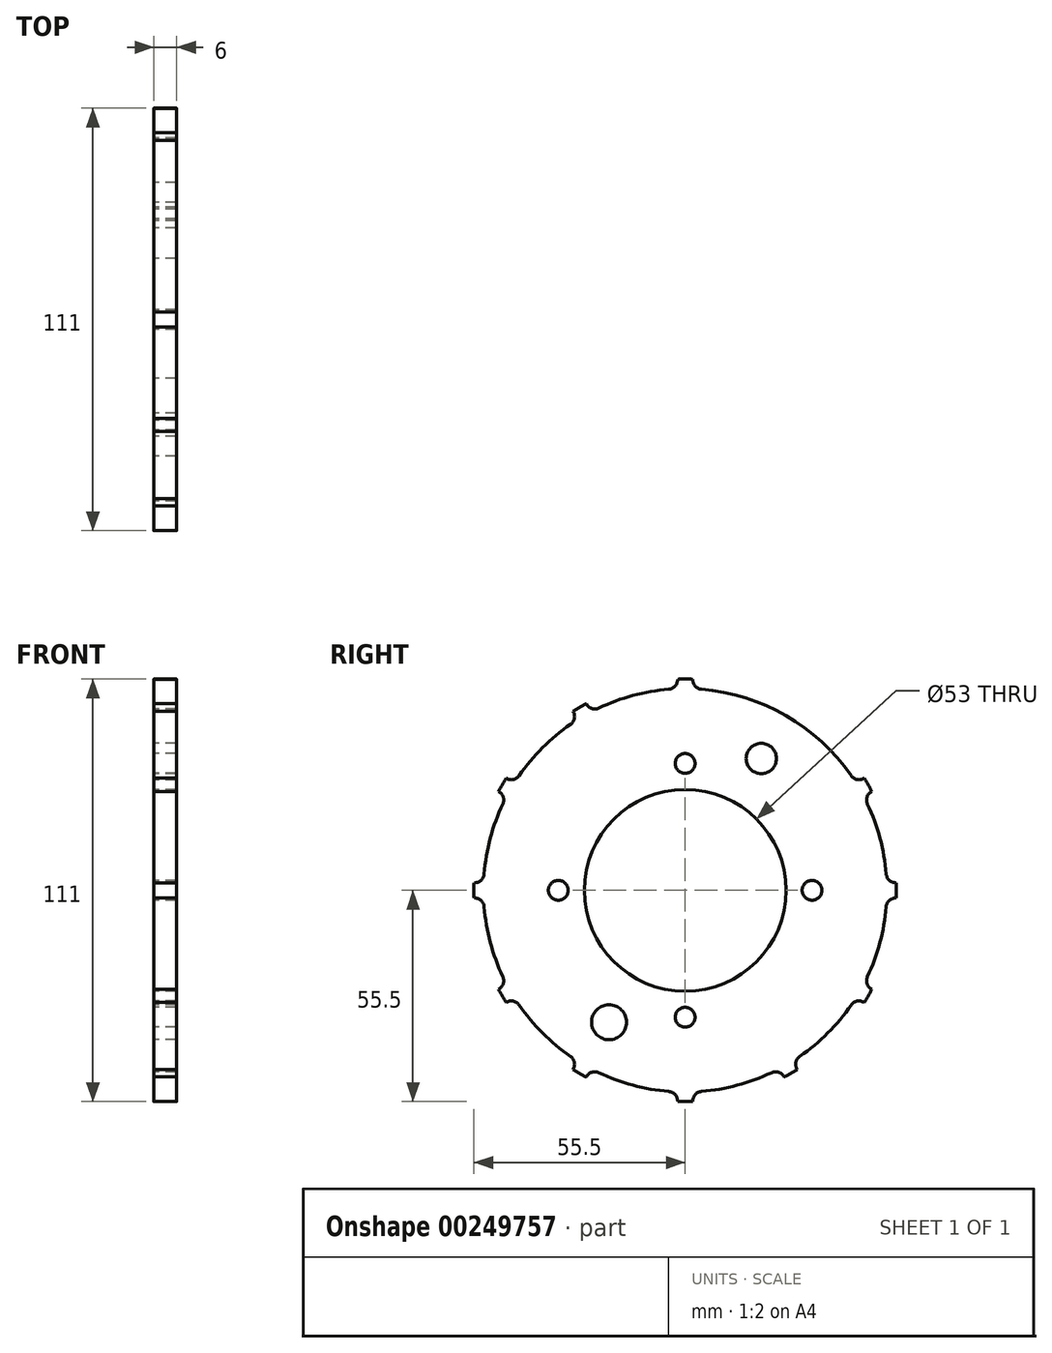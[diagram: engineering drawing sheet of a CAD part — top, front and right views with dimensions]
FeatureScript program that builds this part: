
annotation { "Feature Type Name" : "Feature", "Feature Type Description" : "" }
export const myFeature = defineFeature(function(context is Context, id is Id, definition is map)
    precondition{}
    {
        {
            var Q0;
            Q0=qCreatedBy(makeId("Right.planeOp"),FACE);
            var sketch = newSketch(context, id + "F0", { "sketchPlane" : qUnion([Q0])});
            skCircle(sketch, "E0", {"center": v(0, 0) * mm, "radius": 26.5 * mm});
            skLineSegment(sketch, "E1", {"start": v(0, 6.12) * mm, "end": v(0, -11) * mm, "construction": true});
            skCircle(sketch, "E2", {"center": v(0, 0) * mm, "radius": 53 * mm});
            skLineSegment(sketch, "E3", {"start": v(0, 0) * mm, "end": v(-20, -34.64) * mm, "construction": true});
            skCircle(sketch, "E4", {"center": v(-20, -34.64) * mm, "radius": 4.6 * mm});
            skArc(sketch, "E5", {"start": v(-6.98, 55.06) * mm, "mid": v(-4.3, 52.83) * mm, "end": v(-2, 55.46) * mm});
            skArc(sketch, "E6.1.0", {"start": v(-33.58, 44.2) * mm, "mid": v(-30.13, 43.6) * mm, "end": v(-29.46, 47.03) * mm});
            skArc(sketch, "E6.2.0", {"start": v(-51.17, 21.48) * mm, "mid": v(-47.9, 22.7) * mm, "end": v(-49.03, 26) * mm});
            skArc(sketch, "E6.3.0", {"start": v(-55.06, -6.98) * mm, "mid": v(-52.83, -4.3) * mm, "end": v(-55.46, -2) * mm});
            skArc(sketch, "E6.4.0", {"start": v(-44.2, -33.58) * mm, "mid": v(-43.6, -30.13) * mm, "end": v(-47.03, -29.46) * mm});
            skArc(sketch, "E6.5.0", {"start": v(-21.48, -51.17) * mm, "mid": v(-22.7, -47.9) * mm, "end": v(-26, -49.03) * mm});
            skArc(sketch, "E6.6.0", {"start": v(6.98, -55.06) * mm, "mid": v(4.3, -52.83) * mm, "end": v(2, -55.46) * mm});
            skArc(sketch, "E6.7.0", {"start": v(33.58, -44.2) * mm, "mid": v(30.13, -43.6) * mm, "end": v(29.46, -47.03) * mm});
            skArc(sketch, "E6.8.0", {"start": v(51.17, -21.48) * mm, "mid": v(47.9, -22.7) * mm, "end": v(49.03, -26) * mm});
            skArc(sketch, "E6.9.0", {"start": v(55.06, 6.98) * mm, "mid": v(52.83, 4.3) * mm, "end": v(55.46, 2) * mm});
            skArc(sketch, "E6.10.0", {"start": v(44.2, 33.58) * mm, "mid": v(43.6, 30.13) * mm, "end": v(47.03, 29.46) * mm});
            skArc(sketch, "E6.11.0", {"start": v(21.48, 51.17) * mm, "mid": v(22.7, 47.9) * mm, "end": v(26, 49.03) * mm});
            skCircle(sketch, "E7.converted", {"center": v(0, 0) * mm, "radius": 55.5 * mm});
            skArc(sketch, "E8", {"start": v(2, 55.46) * mm, "mid": v(4.3, 52.83) * mm, "end": v(6.98, 55.06) * mm});
            skArc(sketch, "E9.1.0", {"start": v(-26, 49.03) * mm, "mid": v(-22.7, 47.9) * mm, "end": v(-21.48, 51.17) * mm});
            skArc(sketch, "E9.2.0", {"start": v(-47.03, 29.46) * mm, "mid": v(-43.6, 30.13) * mm, "end": v(-44.2, 33.58) * mm});
            skArc(sketch, "E9.3.0", {"start": v(-55.46, 2) * mm, "mid": v(-52.83, 4.3) * mm, "end": v(-55.06, 6.98) * mm});
            skArc(sketch, "E9.4.0", {"start": v(-49.03, -26) * mm, "mid": v(-47.9, -22.7) * mm, "end": v(-51.17, -21.48) * mm});
            skArc(sketch, "E9.5.0", {"start": v(-29.46, -47.03) * mm, "mid": v(-30.13, -43.6) * mm, "end": v(-33.58, -44.2) * mm});
            skArc(sketch, "E9.6.0", {"start": v(-2, -55.46) * mm, "mid": v(-4.3, -52.83) * mm, "end": v(-6.98, -55.06) * mm});
            skArc(sketch, "E9.7.0", {"start": v(26, -49.03) * mm, "mid": v(22.7, -47.9) * mm, "end": v(21.48, -51.17) * mm});
            skArc(sketch, "E9.8.0", {"start": v(47.03, -29.46) * mm, "mid": v(43.6, -30.13) * mm, "end": v(44.2, -33.58) * mm});
            skArc(sketch, "E9.9.0", {"start": v(55.46, -2) * mm, "mid": v(52.83, -4.3) * mm, "end": v(55.06, -6.98) * mm});
            skArc(sketch, "E9.10.0", {"start": v(49.03, 26) * mm, "mid": v(47.9, 22.7) * mm, "end": v(51.17, 21.48) * mm});
            skArc(sketch, "E9.11.0", {"start": v(29.46, 47.03) * mm, "mid": v(30.13, 43.6) * mm, "end": v(33.58, 44.2) * mm});
            skCircle(sketch, "E10", {"center": v(0, 33.33) * mm, "radius": 2.6 * mm});
            skLineSegment(sketch, "E11", {"start": v(-5.3, 0) * mm, "end": v(6.06, 0) * mm, "construction": true});
            skCircle(sketch, "E12.1.0", {"center": v(-33.33, 0) * mm, "radius": 2.6 * mm});
            skCircle(sketch, "E12.2.0", {"center": v(0, -33.33) * mm, "radius": 2.6 * mm});
            skCircle(sketch, "E12.3.0", {"center": v(33.33, 0) * mm, "radius": 2.6 * mm});
            skCircle(sketch, "E13", {"center": v(20, 34.64) * mm, "radius": 3.99 * mm});
            skSolve(sketch);
        }
        {
            var Q0;
            {var subQ0=sQuery(id+"F0.wireOp",EDGE,"E8");var subQ1=sQuery(id+"F0.wireOp",EDGE,"E2");var subQ2=makeQuery(id+"F0.imprint","INTERSECT",VERTEX,{"derivedFrom":[subQ1,subQ0]});Q0=makeQuery(id+"F0.imprint","IMPRINT",FACE,{"disambiguationData":[TD([[makeQuery(id+"F0.imprint","IMPRINT",EDGE,{"disambiguationData":[TD([[subQ2,-1.0]])],"derivedFrom":subQ1}),-1.0]])]});}
            var Q1;
            {var subQ0=sQuery(id+"F0.wireOp",EDGE,"E9.2.0");var subQ1=sQuery(id+"F0.wireOp",EDGE,"E2");var subQ2=makeQuery(id+"F0.imprint","INTERSECT",VERTEX,{"derivedFrom":[subQ1,subQ0]});Q1=makeQuery(id+"F0.imprint","IMPRINT",FACE,{"disambiguationData":[TD([[makeQuery(id+"F0.imprint","IMPRINT",EDGE,{"disambiguationData":[TD([[subQ2,-1.0]])],"derivedFrom":subQ1}),-1.0]])]});}
            var Q2;
            Q2=makeQuery(id+"F0.imprint","IMPRINT",FACE,{"disambiguationData":[TD([[makeQuery(id+"F0.imprint","IMPRINT",EDGE,{"derivedFrom":sQuery(id+"F0.wireOp",EDGE,"E0")}),-1.0]])]});
            var Q3;
            {var subQ0=sQuery(id+"F0.wireOp",EDGE,"E9.3.0");var subQ1=sQuery(id+"F0.wireOp",EDGE,"E2");var subQ2=makeQuery(id+"F0.imprint","INTERSECT",VERTEX,{"derivedFrom":[subQ1,subQ0]});Q3=makeQuery(id+"F0.imprint","IMPRINT",FACE,{"disambiguationData":[TD([[makeQuery(id+"F0.imprint","IMPRINT",EDGE,{"disambiguationData":[TD([[subQ2,-1.0]])],"derivedFrom":subQ1}),-1.0]])]});}
            var Q4;
            {var subQ0=sQuery(id+"F0.wireOp",EDGE,"E9.4.0");var subQ1=sQuery(id+"F0.wireOp",EDGE,"E2");var subQ2=makeQuery(id+"F0.imprint","INTERSECT",VERTEX,{"derivedFrom":[subQ1,subQ0]});Q4=makeQuery(id+"F0.imprint","IMPRINT",FACE,{"disambiguationData":[TD([[makeQuery(id+"F0.imprint","IMPRINT",EDGE,{"disambiguationData":[TD([[subQ2,-1.0]])],"derivedFrom":subQ1}),-1.0]])]});}
            var Q5;
            {var subQ0=sQuery(id+"F0.wireOp",EDGE,"E9.5.0");var subQ1=sQuery(id+"F0.wireOp",EDGE,"E2");var subQ2=makeQuery(id+"F0.imprint","INTERSECT",VERTEX,{"derivedFrom":[subQ1,subQ0]});Q5=makeQuery(id+"F0.imprint","IMPRINT",FACE,{"disambiguationData":[TD([[makeQuery(id+"F0.imprint","IMPRINT",EDGE,{"disambiguationData":[TD([[subQ2,-1.0]])],"derivedFrom":subQ1}),-1.0]])]});}
            var Q6;
            {var subQ0=sQuery(id+"F0.wireOp",EDGE,"E9.6.0");var subQ1=sQuery(id+"F0.wireOp",EDGE,"E2");var subQ2=makeQuery(id+"F0.imprint","INTERSECT",VERTEX,{"derivedFrom":[subQ1,subQ0]});Q6=makeQuery(id+"F0.imprint","IMPRINT",FACE,{"disambiguationData":[TD([[makeQuery(id+"F0.imprint","IMPRINT",EDGE,{"disambiguationData":[TD([[subQ2,-1.0]])],"derivedFrom":subQ1}),-1.0]])]});}
            var Q7;
            {var subQ0=sQuery(id+"F0.wireOp",EDGE,"E9.7.0");var subQ1=sQuery(id+"F0.wireOp",EDGE,"E2");var subQ2=makeQuery(id+"F0.imprint","INTERSECT",VERTEX,{"derivedFrom":[subQ1,subQ0]});Q7=makeQuery(id+"F0.imprint","IMPRINT",FACE,{"disambiguationData":[TD([[makeQuery(id+"F0.imprint","IMPRINT",EDGE,{"disambiguationData":[TD([[subQ2,-1.0]])],"derivedFrom":subQ1}),-1.0]])]});}
            var Q8;
            {var subQ0=sQuery(id+"F0.wireOp",EDGE,"E9.8.0");var subQ1=sQuery(id+"F0.wireOp",EDGE,"E2");var subQ2=makeQuery(id+"F0.imprint","INTERSECT",VERTEX,{"derivedFrom":[subQ1,subQ0]});Q8=makeQuery(id+"F0.imprint","IMPRINT",FACE,{"disambiguationData":[TD([[makeQuery(id+"F0.imprint","IMPRINT",EDGE,{"disambiguationData":[TD([[subQ2,-1.0]])],"derivedFrom":subQ1}),-1.0]])]});}
            var Q9;
            {var subQ0=sQuery(id+"F0.wireOp",EDGE,"E6.9.0");var subQ1=sQuery(id+"F0.wireOp",EDGE,"E2");var subQ2=makeQuery(id+"F0.imprint","INTERSECT",VERTEX,{"derivedFrom":[subQ1,subQ0]});Q9=makeQuery(id+"F0.imprint","IMPRINT",FACE,{"disambiguationData":[TD([[makeQuery(id+"F0.imprint","IMPRINT",EDGE,{"disambiguationData":[TD([[subQ2,1.0]])],"derivedFrom":subQ1}),-1.0]])]});}
            var Q10;
            {var subQ0=sQuery(id+"F0.wireOp",EDGE,"E9.10.0");var subQ1=sQuery(id+"F0.wireOp",EDGE,"E2");var subQ2=makeQuery(id+"F0.imprint","INTERSECT",VERTEX,{"derivedFrom":[subQ1,subQ0]});Q10=makeQuery(id+"F0.imprint","IMPRINT",FACE,{"disambiguationData":[TD([[makeQuery(id+"F0.imprint","IMPRINT",EDGE,{"disambiguationData":[TD([[subQ2,-1.0]])],"derivedFrom":subQ1}),-1.0]])]});}
            var Q11;
            {var subQ0=sQuery(id+"F0.wireOp",EDGE,"E9.1.0");var subQ1=sQuery(id+"F0.wireOp",EDGE,"E2");var subQ2=makeQuery(id+"F0.imprint","INTERSECT",VERTEX,{"derivedFrom":[subQ1,subQ0]});Q11=makeQuery(id+"F0.imprint","IMPRINT",FACE,{"disambiguationData":[TD([[makeQuery(id+"F0.imprint","IMPRINT",EDGE,{"disambiguationData":[TD([[subQ2,-1.0]])],"derivedFrom":subQ1}),-1.0]])]});}
            extrude(context, id + "F1", {"entities" : qUnion([Q0, Q1, Q2, Q3, Q4, Q5, Q6, Q7, Q8, Q9, Q10, Q11]), "depth" : 6 * mm});
        }
    });
